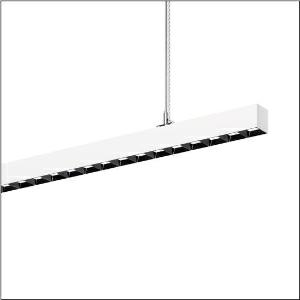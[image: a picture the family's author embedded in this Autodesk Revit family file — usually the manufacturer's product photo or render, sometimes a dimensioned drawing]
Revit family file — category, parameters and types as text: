
# Revit family: silica_r__21_51mx32dc3dwb_4ada
name_source: partatom
category: Lighting Fixtures
units: mm (PartAtom-declared; Revit-internal decimal feet)

## family parameters
Cut with Voids When Loaded = No
Host = Face
Light Source = No
Part Type = Normal
Room Calculation Point = No
Round Connector Dimension = Use Diameter
Shared = No

## types (1)
- --- (1 x LED, 18220 lm, 113 W, 3000K)
    Apparent Load = 113 VA
    CIE Flux Codes = 86 99 100 59 100
    Color Rendering = 80
    Color Temperature = 3000K
    Default Elevation = 1800 mm
    Description = Silica® 21, office luminaire, primary light control with darklight reflector, of PMMA, black, CAT 2 (L<= 3000cd/m²), light emission: direct/indirect distribution, primary light characteristic: symmetric, installation type: suspended mounting, LED, rated luminous flux: 18.220lm, luminous efficacy: 161lm/W, light colour: 830, colour temperature: 3000K, with terminal, 3+2-pole, max. 2.5mm², mains connection: 220..240V, AC, 50/60Hz, rated input power: 113W, luminaire housing, of aluminium, traffic white (RAL 9016), length: 3.004mm, width: 53mm, height: 53mm, protection rating (complete): IP20, insulation class (complete): insulation class I (protective earthing), certification: CE, permissible operating ambient temperature: 0..+35°C, standard: EN 50419, packaging unit: 1 piece
    Height = 53 mm
    Lamp = 1 x LED
    Lamp Light Flux = 18220 lm
    Lamp Power = 113 W
    Lamp count = 1
    Length = 3004 mm
    Luminous efficacy = 161 lm/W
    Manufacturer = Siteco
    ModVariant = No
    Model = 51MX32DC3DWB
    Mounting Place = Ceiling
    Mounting Type = Pendant
    Number of Poles = 1
    OnlyDefault = Yes
    Power Factor = 1
    Product Name = Silica® 21
    Product group = office luminaire | ceiling pendant
    ProductGroupID = 902
    Protection Class = Protection class I
    Protection Degree = IP 20
    RLX_Detail_Level = 1
    RLX_Emergency_Light_Flux = 0 lm
    RLX_Emergency_Type = 0
    RLX_Emergency_Type_DB = No
    RlxData = <blob elided: 65693 chars, md5=5e78ceae>
    Socket = socket
    Standby Power = 0 W
    System Light Flux = 18220 lm
    System Power = 113 W
    Type Comments = factory setting: luminous flux: 100 % | dim-lin: 254 | 391 mA
    Type Image = l_1313619.jpg
    URL = http://relux.com
    VarID = @adj_071047
    Voltage = 0 V
    Weight = 0.00 kg
    Width = 53 mm

## geometry (parser evidence)
native form markers: Blend x4, Sweep x14
no freeform markers — native parametric forms only
